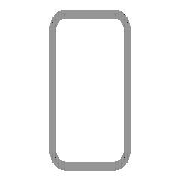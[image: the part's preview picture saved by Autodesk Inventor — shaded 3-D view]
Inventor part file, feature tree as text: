
AUTODESK INVENTOR PART (.ipt)
format: ipt  version: 2025.3 (Build 293356000, 356)  size: 135,168 bytes
history: native  units: mm (DEFAULTED — no unit token found)
features: other x4, sketch x1, plane x1
ambient origin geometry x8: Origin, YZ Plane, XZ Plane, XY Plane, X Axis, Y Axis, Z Axis, Center Point
bodies: Solid1 (feature_tree), Body (feature_tree)
feature tree (6):
  parser-record x1  (decoder bookkeeping rows leaked as tree rows — omitted from the tree; the rows remain in map.json)
  other  "Driven Length"
  other  "Start Plane"
  other  "End Plane"
  sketch  "Sketch3"  dims[d3=255.0mm d4=0.0mm d7=6.0mm d9=40.0mm d11=80.0mm d12=3.0mm d13=20.0mm d14=275.0mm d15=20.0mm d16=40.0mm d17=90.0deg d18=255.0mm]
  plane  "Work Plane3"
